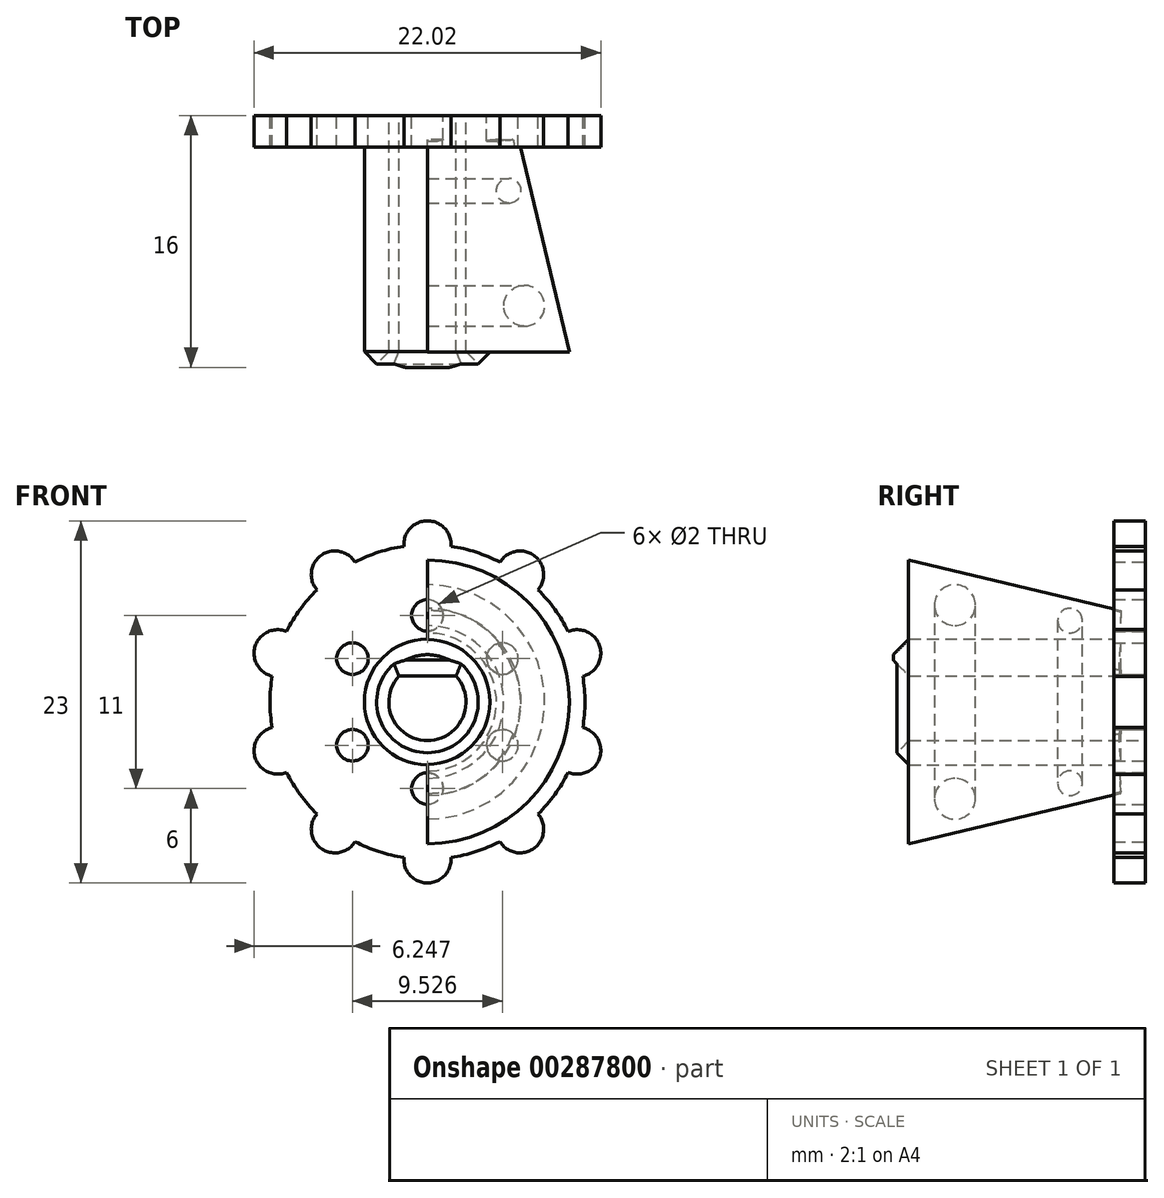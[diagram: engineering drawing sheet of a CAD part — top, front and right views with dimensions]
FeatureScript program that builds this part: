
annotation { "Feature Type Name" : "Feature", "Feature Type Description" : "" }
export const myFeature = defineFeature(function(context is Context, id is Id, definition is map)
    precondition{}
    {
        {
            var Q0;
            Q0=qCreatedBy(makeId("Front.planeOp"),FACE);
            var sketch = newSketch(context, id + "F0", { "sketchPlane" : qUnion([Q0])});
            skCircle(sketch, "E0", {"center": v(0, 0) * mm, "radius": 2.45 * mm});
            skLineSegment(sketch, "E1", {"start": v(-1.81, 1.65) * mm, "end": v(1.81, 1.65) * mm});
            skCircle(sketch, "E2", {"center": v(0, 0) * mm, "radius": 10 * mm});
            skCircle(sketch, "E3", {"center": v(0, 5.5) * mm, "radius": 1 * mm});
            skCircle(sketch, "E4.1.0", {"center": v(-4.76, 2.75) * mm, "radius": 1 * mm});
            skCircle(sketch, "E4.2.0", {"center": v(-4.76, -2.75) * mm, "radius": 1 * mm});
            skCircle(sketch, "E4.3.0", {"center": v(0, -5.5) * mm, "radius": 1 * mm});
            skCircle(sketch, "E4.4.0", {"center": v(4.76, -2.75) * mm, "radius": 1 * mm});
            skCircle(sketch, "E4.5.0", {"center": v(4.76, 2.75) * mm, "radius": 1 * mm});
            skArc(sketch, "E5", {"start": v(1.5, 9.89) * mm, "mid": v(0, 11.5) * mm, "end": v(-1.5, 9.89) * mm});
            skArc(sketch, "E6.1.0", {"start": v(-4.6, 8.88) * mm, "mid": v(-6.76, 9.3) * mm, "end": v(-7.02, 7.12) * mm});
            skArc(sketch, "E6.2.0", {"start": v(-8.94, 4.48) * mm, "mid": v(-10.94, 3.55) * mm, "end": v(-9.87, 1.63) * mm});
            skArc(sketch, "E6.3.0", {"start": v(-9.87, -1.63) * mm, "mid": v(-10.94, -3.55) * mm, "end": v(-8.94, -4.48) * mm});
            skArc(sketch, "E6.4.0", {"start": v(-7.02, -7.12) * mm, "mid": v(-6.76, -9.3) * mm, "end": v(-4.6, -8.88) * mm});
            skArc(sketch, "E6.5.0", {"start": v(-1.5, -9.89) * mm, "mid": v(0, -11.5) * mm, "end": v(1.5, -9.89) * mm});
            skArc(sketch, "E6.6.0", {"start": v(4.6, -8.88) * mm, "mid": v(6.76, -9.3) * mm, "end": v(7.02, -7.12) * mm});
            skArc(sketch, "E6.7.0", {"start": v(8.94, -4.48) * mm, "mid": v(10.94, -3.55) * mm, "end": v(9.87, -1.63) * mm});
            skArc(sketch, "E6.8.0", {"start": v(9.87, 1.63) * mm, "mid": v(10.94, 3.55) * mm, "end": v(8.94, 4.48) * mm});
            skArc(sketch, "E6.9.0", {"start": v(7.02, 7.12) * mm, "mid": v(6.76, 9.3) * mm, "end": v(4.6, 8.88) * mm});
            skSolve(sketch);
        }
        {
            var Q0;
            Q0=makeQuery(id+"F0.imprint","IMPRINT",FACE,{"disambiguationData":[TD([[makeQuery(id+"F0.imprint","IMPRINT",EDGE,{"derivedFrom":sQuery(id+"F0.wireOp",EDGE,"E2")}),1.0]])]});
            var Q1;
            {var subQ0=sQuery(id+"F0.wireOp",EDGE,"E1");Q1=makeQuery(id+"F0.imprint","IMPRINT",FACE,{"disambiguationData":[TD([[makeQuery(id+"F0.imprint","IMPRINT",EDGE,{"derivedFrom":subQ0}),1.0]])]});}
            var Q2;
            {var subQ0=sQuery(id+"F0.wireOp",EDGE,"E5");Q2=makeQuery(id+"F0.imprint","IMPRINT",FACE,{"disambiguationData":[TD([[makeQuery(id+"F0.imprint","IMPRINT",EDGE,{"derivedFrom":subQ0}),1.0]])]});}
            var Q3;
            {var subQ0=sQuery(id+"F0.wireOp",EDGE,"E6.9.0");Q3=makeQuery(id+"F0.imprint","IMPRINT",FACE,{"disambiguationData":[TD([[makeQuery(id+"F0.imprint","IMPRINT",EDGE,{"derivedFrom":subQ0}),1.0]])]});}
            var Q4;
            {var subQ0=sQuery(id+"F0.wireOp",EDGE,"E6.8.0");Q4=makeQuery(id+"F0.imprint","IMPRINT",FACE,{"disambiguationData":[TD([[makeQuery(id+"F0.imprint","IMPRINT",EDGE,{"derivedFrom":subQ0}),1.0]])]});}
            var Q5;
            {var subQ0=sQuery(id+"F0.wireOp",EDGE,"E6.7.0");Q5=makeQuery(id+"F0.imprint","IMPRINT",FACE,{"disambiguationData":[TD([[makeQuery(id+"F0.imprint","IMPRINT",EDGE,{"derivedFrom":subQ0}),1.0]])]});}
            var Q6;
            {var subQ0=sQuery(id+"F0.wireOp",EDGE,"E6.6.0");Q6=makeQuery(id+"F0.imprint","IMPRINT",FACE,{"disambiguationData":[TD([[makeQuery(id+"F0.imprint","IMPRINT",EDGE,{"derivedFrom":subQ0}),1.0]])]});}
            var Q7;
            {var subQ0=sQuery(id+"F0.wireOp",EDGE,"E6.5.0");Q7=makeQuery(id+"F0.imprint","IMPRINT",FACE,{"disambiguationData":[TD([[makeQuery(id+"F0.imprint","IMPRINT",EDGE,{"derivedFrom":subQ0}),1.0]])]});}
            var Q8;
            {var subQ0=sQuery(id+"F0.wireOp",EDGE,"E6.4.0");Q8=makeQuery(id+"F0.imprint","IMPRINT",FACE,{"disambiguationData":[TD([[makeQuery(id+"F0.imprint","IMPRINT",EDGE,{"derivedFrom":subQ0}),1.0]])]});}
            var Q9;
            {var subQ0=sQuery(id+"F0.wireOp",EDGE,"E6.3.0");Q9=makeQuery(id+"F0.imprint","IMPRINT",FACE,{"disambiguationData":[TD([[makeQuery(id+"F0.imprint","IMPRINT",EDGE,{"derivedFrom":subQ0}),1.0]])]});}
            var Q10;
            {var subQ0=sQuery(id+"F0.wireOp",EDGE,"E6.2.0");Q10=makeQuery(id+"F0.imprint","IMPRINT",FACE,{"disambiguationData":[TD([[makeQuery(id+"F0.imprint","IMPRINT",EDGE,{"derivedFrom":subQ0}),1.0]])]});}
            var Q11;
            {var subQ0=sQuery(id+"F0.wireOp",EDGE,"E6.1.0");Q11=makeQuery(id+"F0.imprint","IMPRINT",FACE,{"disambiguationData":[TD([[makeQuery(id+"F0.imprint","IMPRINT",EDGE,{"derivedFrom":subQ0}),1.0]])]});}
            extrude(context, id + "F1", {"entities" : qUnion([Q0, Q1, Q2, Q3, Q4, Q5, Q6, Q7, Q8, Q9, Q10, Q11]), "depth" : 2 * mm});
        }
        {
            var Q0;
            Q0=makeQuery(id+"F1.opExtrude","CAP_FACE",FACE,{"disambiguationData":[OSD([sQuery(id+"F0.wireOp",EDGE,"E0"),sQuery(id+"F0.wireOp",EDGE,"E1"),sQuery(id+"F0.wireOp",EDGE,"E2")])],"isStart":false});
            var sketch = newSketch(context, id + "F2", { "sketchPlane" : qUnion([Q0])});
            skCircle(sketch, "E7", {"center": v(0, 0) * mm, "radius": 2.45 * mm});
            skCircle(sketch, "E8", {"center": v(0, 0) * mm, "radius": 4 * mm});
            skLineSegment(sketch, "E9", {"start": v(-1.81, 1.65) * mm, "end": v(1.81, 1.65) * mm});
            skSolve(sketch);
        }
        {
            var Q0;
            Q0=makeQuery(id+"F2.imprint","IMPRINT",FACE,{"disambiguationData":[TD([[makeQuery(id+"F2.imprint","IMPRINT",EDGE,{"derivedFrom":sQuery(id+"F2.wireOp",EDGE,"E8")}),1.0]])]});
            var Q1;
            {var subQ0=sQuery(id+"F2.wireOp",EDGE,"E9");Q1=makeQuery(id+"F2.imprint","IMPRINT",FACE,{"disambiguationData":[TD([[makeQuery(id+"F2.imprint","IMPRINT",EDGE,{"derivedFrom":subQ0}),1.0]])]});}
            extrude(context, id + "F3", {"entities" : qUnion([Q0, Q1]), "operationType" : NewBodyOperationType.ADD, "depth" : 14 * mm});
        }
        {
            var Q0;
            Q0=makeQuery(id+"F3.opExtrude","CAP_FACE",FACE,{"disambiguationData":[OSD([sQuery(id+"F2.wireOp",EDGE,"E7"),sQuery(id+"F2.wireOp",EDGE,"E8"),sQuery(id+"F2.wireOp",EDGE,"E9")])],"isStart":false});
            chamfer(context, id + "F4", {"entities" : qUnion([Q0]), "width" : 1 * mm, "tangentPropagation" : true});
        }
        {
            var Q0;
            Q0=qCreatedBy(makeId("Right.planeOp"),FACE);
            var sketch = newSketch(context, id + "F5", { "sketchPlane" : qUnion([Q0])});
            skLineSegment(sketch, "E10", {"start": v(-1.7, 3.58) * mm, "end": v(-15.03, 3.58) * mm});
            skLineSegment(sketch, "E11", {"start": v(-15.03, 3.58) * mm, "end": v(-15.03, 9.01) * mm});
            skLineSegment(sketch, "E12", {"start": v(-15.03, 9.01) * mm, "end": v(-1.53, 5.8) * mm});
            skLineSegment(sketch, "E13", {"start": v(-1.53, 5.8) * mm, "end": v(-1.7, 3.58) * mm});
            skCircle(sketch, "E14", {"center": v(-4.78, 5.17) * mm, "radius": 0.78 * mm});
            skCircle(sketch, "E15", {"center": v(-12.09, 6.15) * mm, "radius": 1.3 * mm});
            skSolve(sketch);
        }
        {
            var Q0;
            Q0=makeQuery(id+"F5.imprint","IMPRINT",FACE,{"disambiguationData":[TD([[makeQuery(id+"F5.imprint","IMPRINT",EDGE,{"derivedFrom":sQuery(id+"F5.wireOp",EDGE,"E10")}),-1.0]])]});
            var Q1;
            Q1=makeQuery(id+"F3.opExtrude","SWEPT_FACE",FACE,{"disambiguationData":[OSD([sQuery(id+"F2.wireOp",EDGE,"E8")])]});
            revolve(context, id + "F6", {"operationType" : NewBodyOperationType.ADD, "entities" : qUnion([Q0]), "axis" : qUnion([Q1]), "revolveType" : RevolveType.ONE_DIRECTION, "angle" : 180 * degree});
        }
    });
